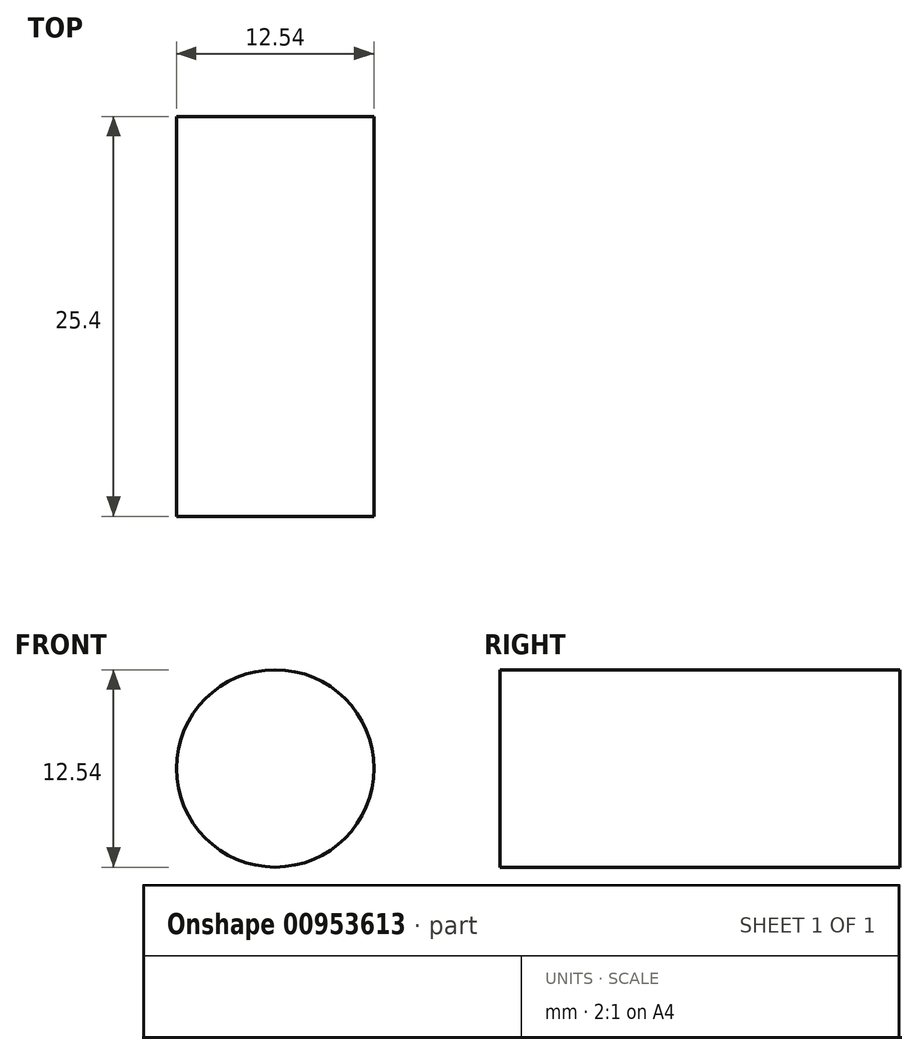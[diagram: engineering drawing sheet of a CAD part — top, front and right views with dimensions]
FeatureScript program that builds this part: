
annotation { "Feature Type Name" : "Feature", "Feature Type Description" : "" }
export const myFeature = defineFeature(function(context is Context, id is Id, definition is map)
    precondition{}
    {
        {
            var Q0;
            Q0=qCreatedBy(makeId("Front.planeOp"),FACE);
            var sketch = newSketch(context, id + "F0", { "sketchPlane" : qUnion([Q0])});
            skCircle(sketch, "E0", {"center": v(0, 0) * mm, "radius": 6.27 * mm});
            skSolve(sketch);
        }
        {
            var Q0;
            Q0=sQuery(id+"F0.wireOp",EDGE,"E0");
            extrude(context, id + "F1", {"bodyType" : ToolBodyType.SURFACE, "surfaceEntities" : qUnion([Q0]), "depth" : 25.4 * mm, "offsetDistance" : 25.4 * mm});
        }
    });
